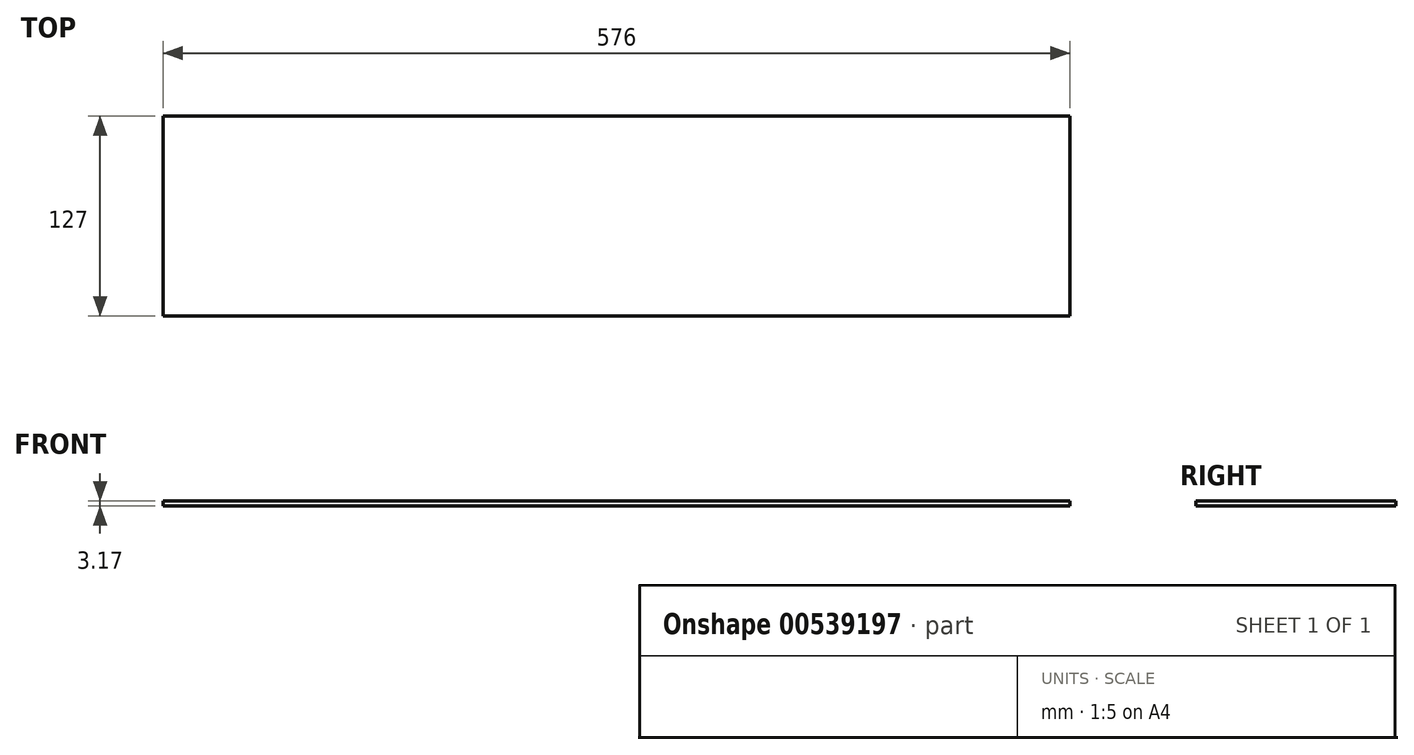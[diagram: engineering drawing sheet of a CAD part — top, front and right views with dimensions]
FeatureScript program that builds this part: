
annotation { "Feature Type Name" : "Feature", "Feature Type Description" : "" }
export const myFeature = defineFeature(function(context is Context, id is Id, definition is map)
    precondition{}
    {
        {
            var Q0;
            Q0=qCreatedBy(makeId("Top.planeOp"),FACE);
            var sketch = newSketch(context, id + "F0", { "sketchPlane" : qUnion([Q0])});
            skLineSegment(sketch, "E0.bottom", {"start": v(-109.9, -63.58) * mm, "end": v(466.1, -63.58) * mm});
            skLineSegment(sketch, "E0.top", {"start": v(-109.9, 63.42) * mm, "end": v(466.1, 63.42) * mm});
            skLineSegment(sketch, "E0.left", {"start": v(-109.9, -63.58) * mm, "end": v(-109.9, 63.42) * mm});
            skLineSegment(sketch, "E0.right", {"start": v(466.1, -63.58) * mm, "end": v(466.1, 63.42) * mm});
            skSolve(sketch);
        }
        {
            var Q0;
            Q0 = qSketchRegion(id + "F0", true);
            extrude(context, id + "F1", {"entities" : qUnion([Q0]), "depth" : 3.17 * mm, "offsetDistance" : 25.4 * mm});
        }
    });
